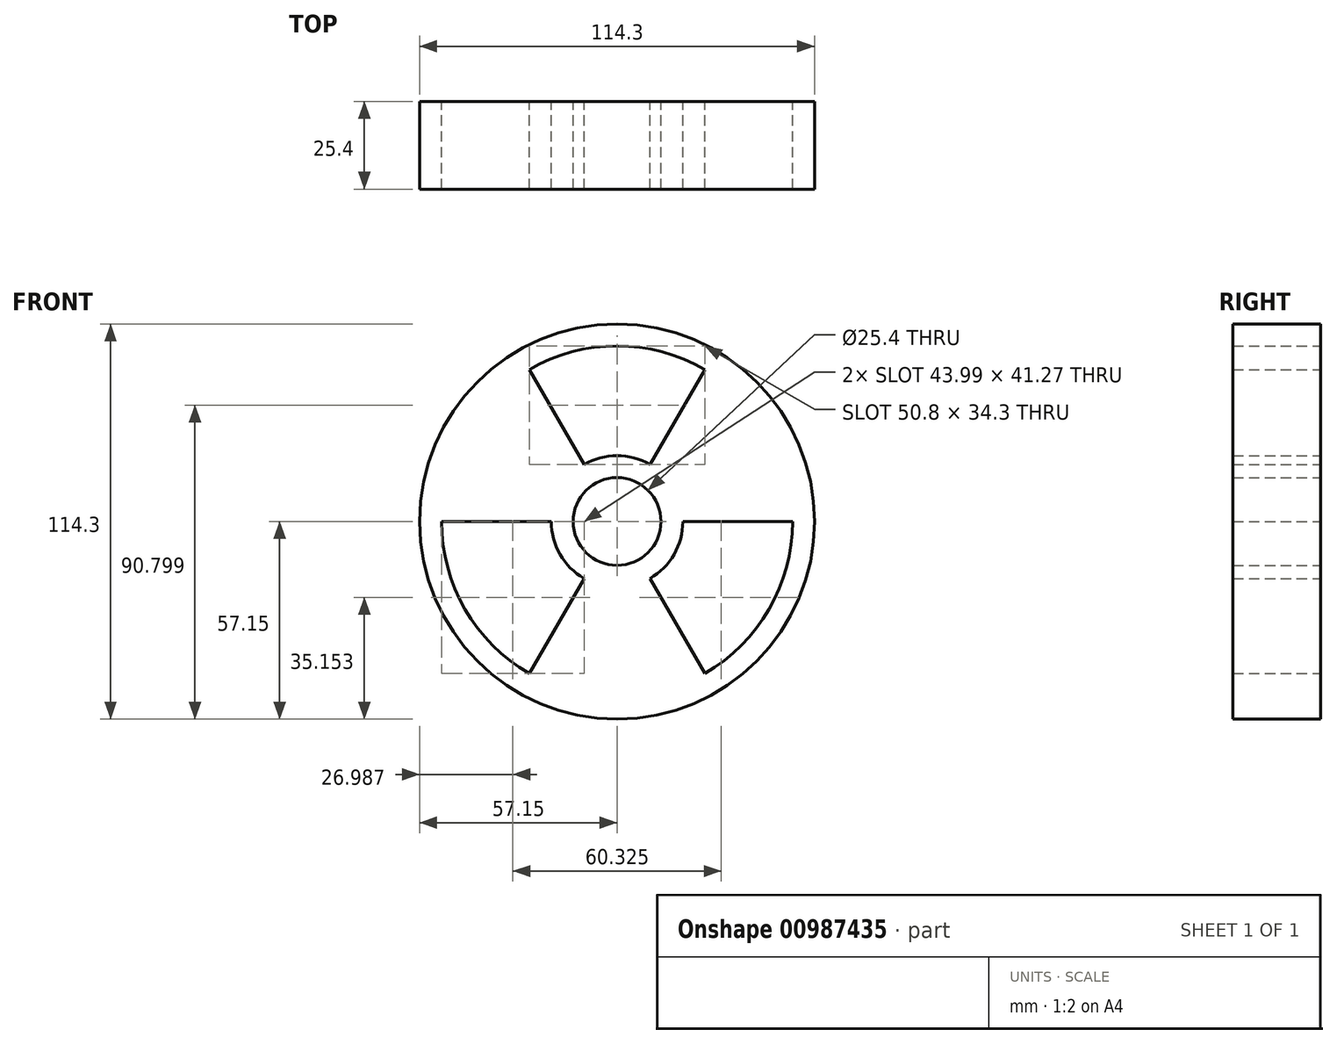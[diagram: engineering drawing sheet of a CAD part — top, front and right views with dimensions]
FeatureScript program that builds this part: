
annotation { "Feature Type Name" : "Feature", "Feature Type Description" : "" }
export const myFeature = defineFeature(function(context is Context, id is Id, definition is map)
    precondition{}
    {
        {
            var Q0;
            Q0=qCreatedBy(makeId("Front.planeOp"),FACE);
            var sketch = newSketch(context, id + "F0", { "sketchPlane" : qUnion([Q0])});
            skLineSegment(sketch, "E0", {"start": v(0, 0) * mm, "end": v(0, 50.8) * mm});
            skLineSegment(sketch, "E1", {"start": v(0, 0) * mm, "end": v(-44, -25.4) * mm, "construction": true});
            skLineSegment(sketch, "E2", {"start": v(0, 0) * mm, "end": v(44, -25.4) * mm});
            skArc(sketch, "E3", {"start": v(-50.8, 0) * mm, "mid": v(-44, -25.4) * mm, "end": v(-25.4, -44) * mm});
            skArc(sketch, "E4", {"start": v(-19.05, 0) * mm, "mid": v(-16.5, -9.53) * mm, "end": v(-9.52, -16.5) * mm});
            skLineSegment(sketch, "E5", {"start": v(-9.53, 16.5) * mm, "end": v(-25.4, 44) * mm});
            skLineSegment(sketch, "E6", {"start": v(9.52, 16.5) * mm, "end": v(25.4, 44) * mm});
            skLineSegment(sketch, "E7", {"start": v(19.05, 0) * mm, "end": v(50.8, 0) * mm});
            skLineSegment(sketch, "E8", {"start": v(9.53, -16.5) * mm, "end": v(25.4, -44) * mm});
            skLineSegment(sketch, "E9", {"start": v(-9.52, -16.5) * mm, "end": v(-25.4, -44) * mm});
            skLineSegment(sketch, "E10", {"start": v(-19.05, 0) * mm, "end": v(-50.8, 0) * mm});
            skArc(sketch, "E11.trimOffspring", {"start": v(9.53, -16.5) * mm, "mid": v(16.5, -9.52) * mm, "end": v(19.05, 0) * mm});
            skArc(sketch, "E12.trimOffspring", {"start": v(9.52, 16.5) * mm, "mid": v(0, 19.05) * mm, "end": v(-9.53, 16.5) * mm});
            skCircle(sketch, "E13", {"center": v(0, 0) * mm, "radius": 12.7 * mm});
            skCircle(sketch, "E14", {"center": v(0, 0) * mm, "radius": 57.15 * mm});
            skArc(sketch, "E15.trimOffspring", {"start": v(25.4, 44) * mm, "mid": v(0, 50.8) * mm, "end": v(-25.4, 44) * mm});
            skArc(sketch, "E16.trimOffspring", {"start": v(25.4, -44) * mm, "mid": v(44, -25.4) * mm, "end": v(50.8, 0) * mm});
            skSolve(sketch);
        }
        {
            var Q0;
            Q0 = qSketchRegion(id + "F0", true);
            extrude(context, id + "F1", {"entities" : qUnion([Q0]), "depth" : 25.4 * mm, "offsetDistance" : 25.4 * mm});
        }
    });
